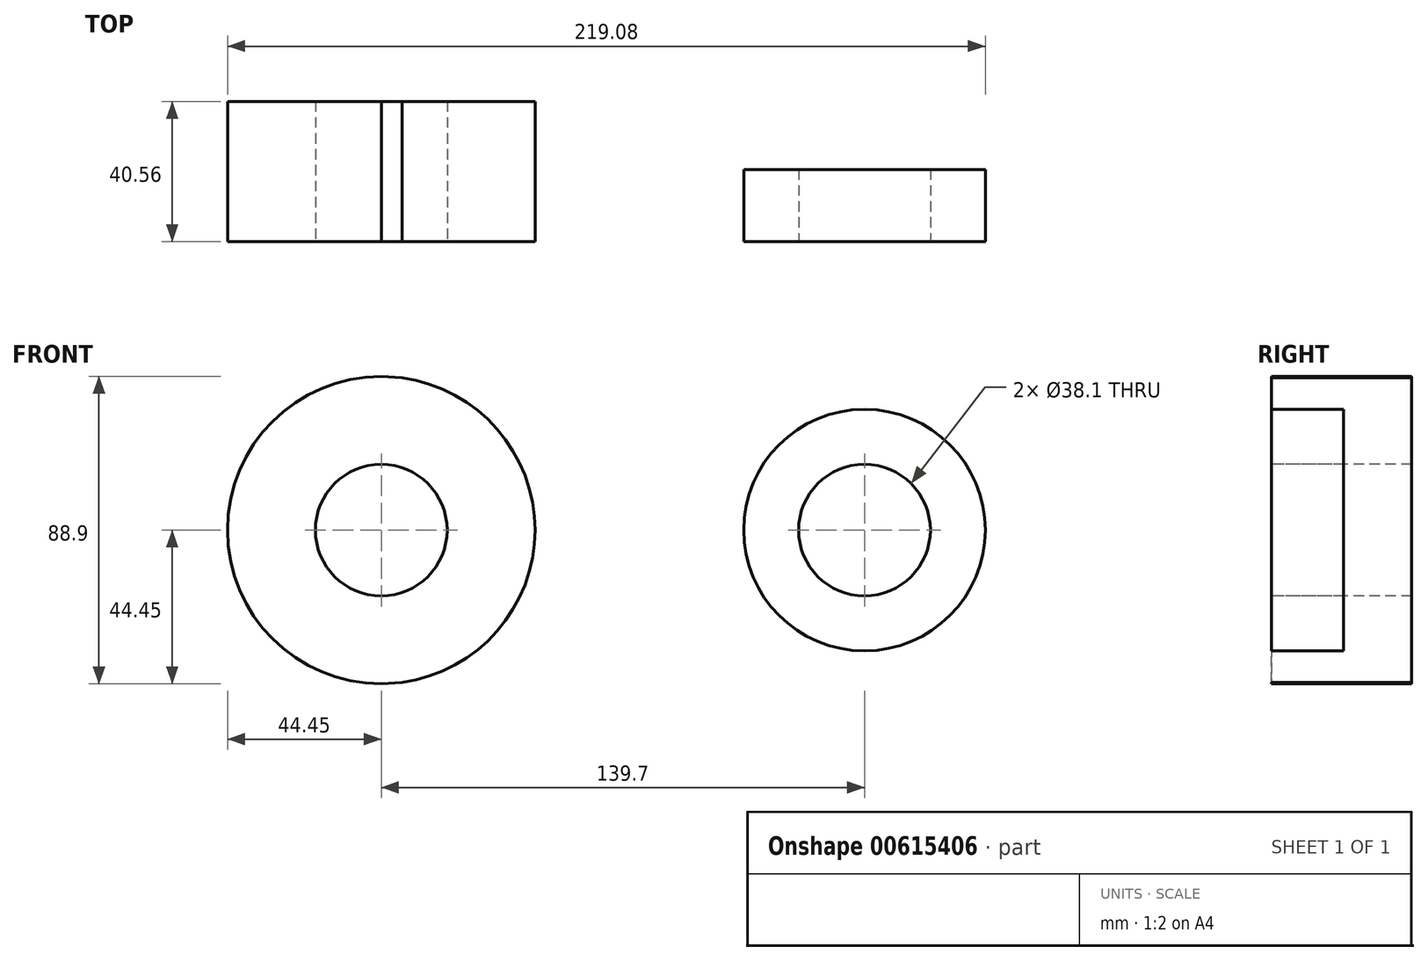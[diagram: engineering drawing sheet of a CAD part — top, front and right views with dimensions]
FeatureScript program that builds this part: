
annotation { "Feature Type Name" : "Feature", "Feature Type Description" : "" }
export const myFeature = defineFeature(function(context is Context, id is Id, definition is map)
    precondition{}
    {
        {
            var Q0;
            Q0=qCreatedBy(makeId("Front.planeOp"),FACE);
            var sketch = newSketch(context, id + "F0", { "sketchPlane" : qUnion([Q0])});
            skCircle(sketch, "E0", {"center": v(0, 0) * mm, "radius": 44.45 * mm});
            skCircle(sketch, "E1", {"center": v(139.7, 0) * mm, "radius": 34.93 * mm});
            skLineSegment(sketch, "E2", {"start": v(0, 44.45) * mm, "end": v(142.06, 34.85) * mm});
            skLineSegment(sketch, "E3", {"start": v(0, -44.45) * mm, "end": v(142.06, -34.85) * mm});
            skCircle(sketch, "E4", {"center": v(0, 0) * mm, "radius": 19.05 * mm});
            skCircle(sketch, "E5", {"center": v(139.7, 0) * mm, "radius": 19.05 * mm});
            skSolve(sketch);
        }
        {
            var Q0;
            Q0=makeQuery(id+"F0.imprint","IMPRINT",FACE,{"disambiguationData":[TD([[makeQuery(id+"F0.imprint","IMPRINT",EDGE,{"derivedFrom":sQuery(id+"F0.wireOp",EDGE,"E4")}),-1.0]])]});
            var Q1;
            {var subQ0=sQuery(id+"F0.wireOp",EDGE,"E2");var subQ1=sQuery(id+"F0.wireOp",EDGE,"E0");var subQ2=makeQuery(id+"F0.imprint","INTERSECT",VERTEX,{"disambiguationData":[OD(1.0)],"derivedFrom":[subQ1,subQ0]});Q1=makeQuery(id+"F0.imprint","IMPRINT",FACE,{"disambiguationData":[TD([[makeQuery(id+"F0.imprint","IMPRINT",EDGE,{"disambiguationData":[TD([[subQ2,1.0]])],"derivedFrom":subQ1}),-1.0]])]});}
            var Q2;
            Q2=makeQuery(id+"F0.imprint","IMPRINT",FACE,{"disambiguationData":[TD([[makeQuery(id+"F0.imprint","IMPRINT",EDGE,{"derivedFrom":sQuery(id+"F0.wireOp",EDGE,"E5")}),-1.0]])]});
            extrude(context, id + "F1", {"entities" : qUnion([Q0, Q1, Q2]), "oppositeDirection" : true, "depth" : 20.87 * mm, "offsetDistance" : 25.4 * mm});
        }
        {
            var Q0;
            Q0=makeQuery(id+"F0.imprint","IMPRINT",FACE,{"disambiguationData":[TD([[makeQuery(id+"F0.imprint","IMPRINT",EDGE,{"derivedFrom":sQuery(id+"F0.wireOp",EDGE,"E4")}),-1.0]])]});
            extrude(context, id + "F2", {"entities" : qUnion([Q0]), "operationType" : NewBodyOperationType.ADD, "oppositeDirection" : true, "depth" : 40.56 * mm, "offsetDistance" : 25.4 * mm});
        }
        {
            var Q0;
            Q0=sQuery(id+"F0.wireOp",EDGE,"E5");
            var Q1;
            Q1=sQuery(id+"F0.wireOp",EDGE,"E4");
            extrude(context, id + "F3", {"bodyType" : ToolBodyType.SURFACE, "surfaceEntities" : qUnion([Q0, Q1]), "depth" : 13.87 * mm, "offsetDistance" : 25.4 * mm});
        }
    });
